# Revit family: Side Opening_2 Panels
name_source: partatom
category: Generic Models
units: mm (PartAtom-declared; Revit-internal decimal feet)

## family parameters
Always vertical = Yes
Can host rebar = No
Cut with Voids When Loaded = No
Part Type = Normal
Room Calculation Point = No
Round Connector Dimension = Use Diameter
Shared = No
Work Plane-Based = No

## types (1)
- Side Opening_2 Panels
    Car Door Operator Brand = BCA
    Car Door Operator Model = BCA44
    Default Elevation = 0 mm  [stored 0 ft]
    Door Height = 2150 mm
    Door Width = 1000 mm  [stored 3.28084 ft]
    DoorLockOpenableFromPit = Yes
    Light Curtain = Yes
    Light Curtain/Photocell Brand = BCA
    Light Curtain/Photocell Model = Bca888
    Mechanical Safety Edge = Yes
    Number of Panels = 2
    OperationType = Not vertically Sliding, side opening
    Photocell = Yes
    door thickness = 60 mm  [stored 0.19685 ft]
    frame thickness = 61 mm  [stored 0.200131 ft]
    framing width = 12 mm  [stored 0.0393701 ft]
    header frame thickness = 20 mm  [stored 0.0656168 ft]
    header thickness = 60 mm  [stored 0.19685 ft]
    header width = 3000 mm  [stored 9.84252 ft]
    sill thickness = 60 mm  [stored 0.19685 ft]
    sill track gap = 16 mm  [stored 0.0524934 ft]
    sill-track width = 22 mm  [stored 0.0721785 ft]
    track width = 3000 mm  [stored 9.84252 ft]

note: [stored X ft] marks values corroborated as IEEE doubles in the binary element streams (Revit-internal decimal feet)

## geometry (parser evidence)
native form markers: Sweep x3
no freeform markers — native parametric forms only
